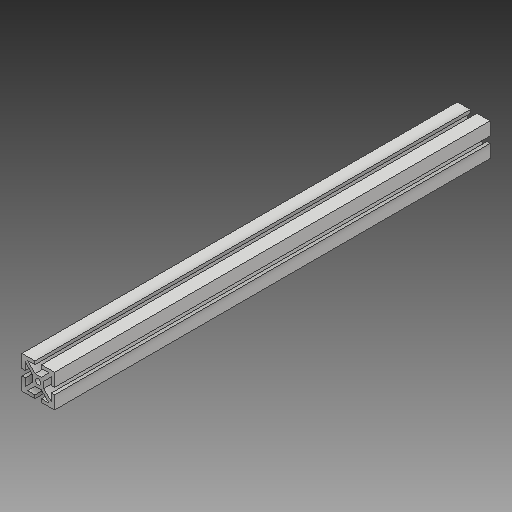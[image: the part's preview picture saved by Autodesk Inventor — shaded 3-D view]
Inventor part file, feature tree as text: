
AUTODESK INVENTOR PART (.ipt)
format: ipt  version: 2018 (Build 220112000, 112)  size: 148,992 bytes
history: native  units: mm
features: extrude x1, sketch x1
ambient origin geometry x8: Origin, YZ Plane, XZ Plane, XY Plane, X Axis, Y Axis, Z Axis, Center Point
bodies: Volumenkörper1 (feature_tree)
feature tree (2):
  extrude  "Extrusion1"  Depth=3.0mm
  sketch  "Skizze1"  dims[d0=3.0mm d1=3.0mm d2=0.5mm d3=1.0mm d4=1.0mm d5=1.2mm d6=1.2mm d7=1.2mm d8=1.2mm d9=0.3mm d10=0.15mm d11=0.15mm d12=0.15mm d13=0.15mm d14=40.0mm d15=0.0mm]
